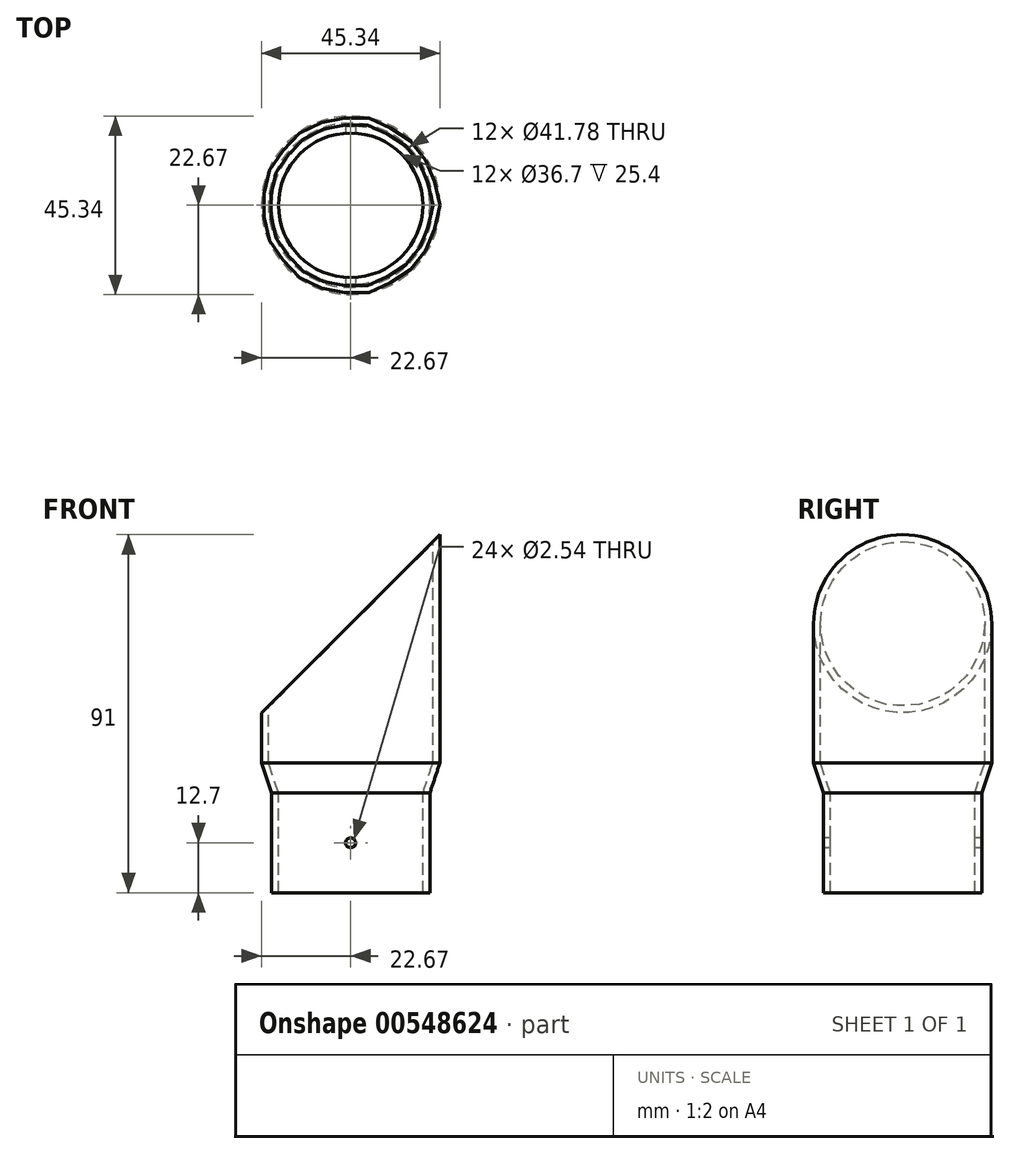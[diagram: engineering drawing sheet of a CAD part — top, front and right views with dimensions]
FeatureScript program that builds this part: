
annotation { "Feature Type Name" : "Feature", "Feature Type Description" : "" }
export const myFeature = defineFeature(function(context is Context, id is Id, definition is map)
    precondition{}
    {
        {
            var Q0;
            Q0=qCreatedBy(makeId("Front.planeOp"),FACE);
            var sketch = newSketch(context, id + "F0", { "sketchPlane" : qUnion([Q0])});
            skLineSegment(sketch, "E0", {"start": v(18.35, -25.4) * mm, "end": v(20.13, -25.4) * mm});
            skLineSegment(sketch, "E1", {"start": v(20.13, -25.4) * mm, "end": v(20.13, 0) * mm});
            skLineSegment(sketch, "E2", {"start": v(20.13, 0) * mm, "end": v(22.67, 7.62) * mm});
            skLineSegment(sketch, "E3", {"start": v(22.67, 7.62) * mm, "end": v(22.67, 66.04) * mm});
            skLineSegment(sketch, "E4", {"start": v(22.67, 66.04) * mm, "end": v(20.9, 66.04) * mm});
            skLineSegment(sketch, "E5", {"start": v(20.9, 66.04) * mm, "end": v(20.9, 7.62) * mm});
            skLineSegment(sketch, "E6", {"start": v(20.9, 7.62) * mm, "end": v(18.35, 0) * mm});
            skLineSegment(sketch, "E7", {"start": v(18.35, 0) * mm, "end": v(18.35, -25.4) * mm});
            skSolve(sketch);
        }
        {
            var Q0;
            Q0=qCreatedBy(makeId("Front.planeOp"),FACE);
            var sketch = newSketch(context, id + "F1", { "sketchPlane" : qUnion([Q0])});
            skLineSegment(sketch, "E8", {"start": v(0, 36.74) * mm, "end": v(0, -22.8) * mm});
            skSolve(sketch);
        }
        {
            var Q0;
            Q0 = qSketchRegion(id + "F1", true);
            var Q1;
            Q1 = qSketchRegion(id + "F0", true);
            var Q2;
            Q2=sQuery(id+"F1.wireOp",EDGE,"E8");
            revolve(context, id + "F2", {"entities" : qUnion([Q0, Q1]), "axis" : qUnion([Q2]), "revolveType" : RevolveType.FULL});
        }
        {
            var Q0;
            Q0=qCreatedBy(makeId("Front.planeOp"),FACE);
            var sketch = newSketch(context, id + "F3", { "sketchPlane" : qUnion([Q0])});
            skLineSegment(sketch, "E9", {"start": v(-23.88, 19.05) * mm, "end": v(103.12, 146.05) * mm});
            skLineSegment(sketch, "E10", {"start": v(103.12, 146.05) * mm, "end": v(-23.88, 146.05) * mm});
            skLineSegment(sketch, "E11", {"start": v(-23.88, 146.05) * mm, "end": v(-23.88, 19.05) * mm});
            skSolve(sketch);
        }
        {
            var Q0;
            Q0=makeQuery(id+"F3.imprint","IMPRINT",FACE,{"disambiguationData":[TD([[makeQuery(id+"F3.imprint","IMPRINT",EDGE,{"derivedFrom":sQuery(id+"F3.wireOp",EDGE,"E9")}),1.0]])]});
            extrude(context, id + "F4", {"entities" : qUnion([Q0]), "operationType" : NewBodyOperationType.REMOVE, "endBound" : BoundingType.SYMMETRIC, "depth" : 101.6 * mm, "offsetDistance" : 25.4 * mm});
        }
        {
            var Q0;
            Q0=qCreatedBy(makeId("Front.planeOp"),FACE);
            var sketch = newSketch(context, id + "F5", { "sketchPlane" : qUnion([Q0])});
            skCircle(sketch, "E12", {"center": v(0, -12.7) * mm, "radius": 1.27 * mm});
            skSolve(sketch);
        }
        {
            var Q0;
            Q0=makeQuery(id+"F5.imprint","IMPRINT",FACE,{"disambiguationData":[TD([[makeQuery(id+"F5.imprint","IMPRINT",EDGE,{"derivedFrom":sQuery(id+"F5.wireOp",EDGE,"E12")}),1.0]])]});
            extrude(context, id + "F6", {"entities" : qUnion([Q0]), "operationType" : NewBodyOperationType.REMOVE, "endBound" : BoundingType.SYMMETRIC, "oppositeDirection" : true, "depth" : 50.8 * mm, "offsetDistance" : 25.4 * mm});
        }
    });
